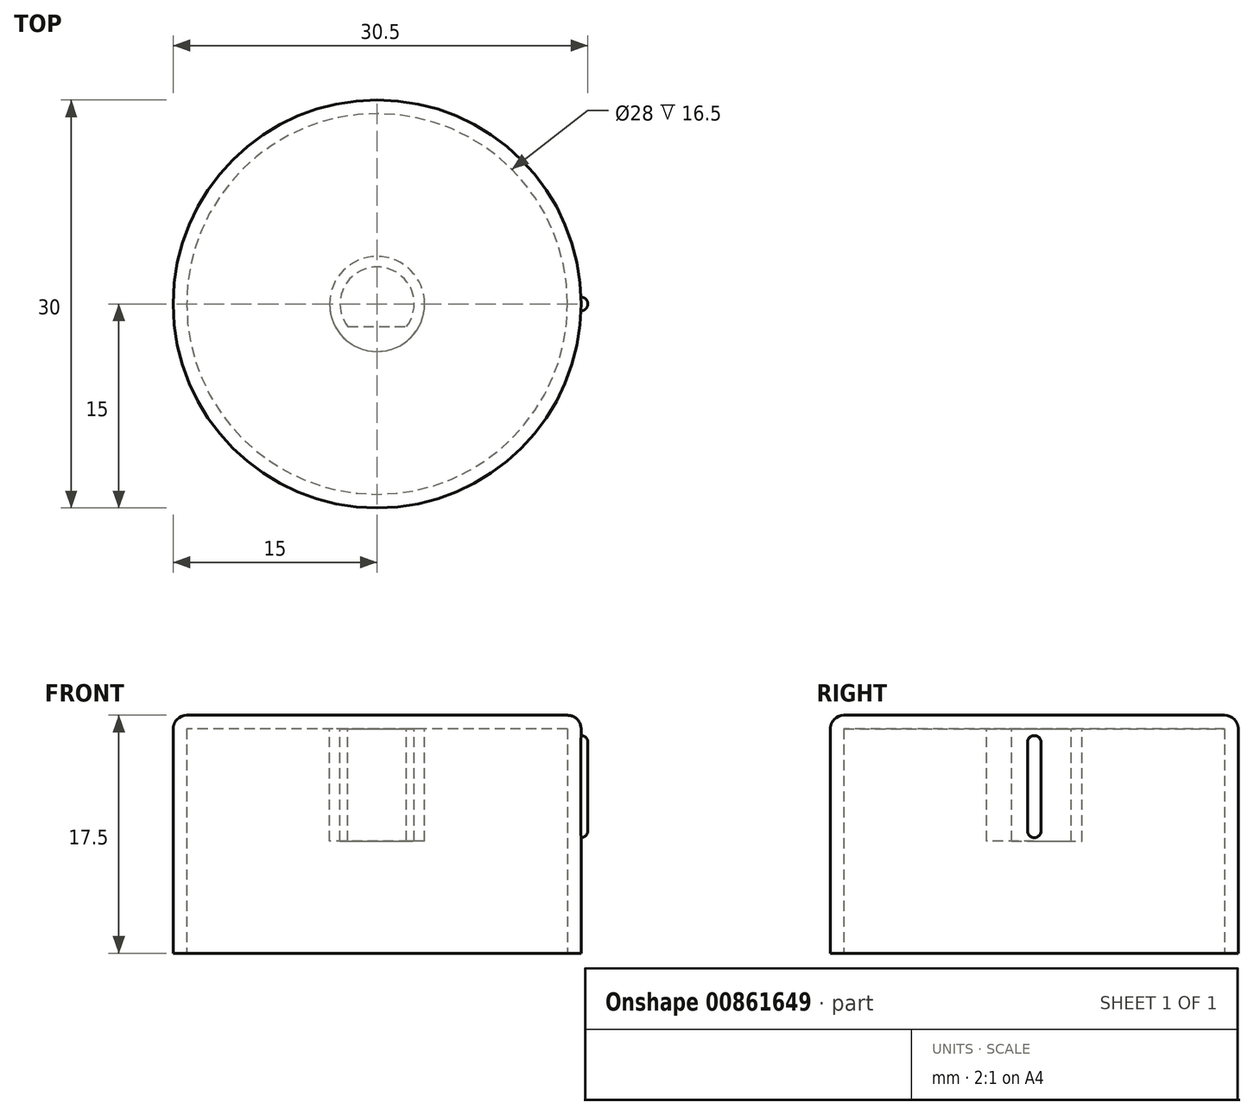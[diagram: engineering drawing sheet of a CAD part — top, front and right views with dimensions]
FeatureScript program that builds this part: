
annotation { "Feature Type Name" : "Feature", "Feature Type Description" : "" }
export const myFeature = defineFeature(function(context is Context, id is Id, definition is map)
    precondition{}
    {
        {
            var Q0;
            Q0=qCreatedBy(makeId("Top.planeOp"),FACE);
            var sketch = newSketch(context, id + "F0", { "sketchPlane" : qUnion([Q0])});
            skCircle(sketch, "E0", {"center": v(0, 0) * mm, "radius": 15 * mm});
            skSolve(sketch);
        }
        {
            var Q0;
            Q0 = qSketchRegion(id + "F0", true);
            extrude(context, id + "F1", {"entities" : qUnion([Q0]), "depth" : 17.5 * mm, "offsetDistance" : 25 * mm});
        }
        {
            var Q0;
            Q0=makeQuery(id+"F1.opExtrude","CAP_FACE",FACE,{"disambiguationData":[OSD([sQuery(id+"F0.wireOp",EDGE,"E0")])],"isStart":true});
            shell(context, id + "F2", {"entities" : qUnion([Q0]), "thickness" : 1 * mm});
        }
        {
            var Q0;
            {var subQ0=sQuery(id+"F0.wireOp",EDGE,"E0");Q0=makeQuery(id+"F2.opShell","OFFSET_FACE",FACE,{"disambiguationData":[OSD([subQ0]),TDD([makeQuery(id+"F1.opExtrude","CAP_FACE",FACE,{"disambiguationData":[OSD([subQ0])],"isStart":false})])]});}
            var sketch = newSketch(context, id + "F3", { "sketchPlane" : qUnion([Q0])});
            skCircle(sketch, "E1", {"center": v(0, 0) * mm, "radius": 3.5 * mm});
            skArc(sketch, "E2", {"start": v(-2.15, 1.67) * mm, "mid": v(0, -2.73) * mm, "end": v(2.15, 1.67) * mm});
            skLineSegment(sketch, "E3", {"start": v(-2.15, 1.67) * mm, "end": v(2.15, 1.67) * mm});
            skSolve(sketch);
        }
        {
            var Q0;
            Q0=makeQuery(id+"F3.imprint","IMPRINT",FACE,{"disambiguationData":[TD([[makeQuery(id+"F3.imprint","IMPRINT",EDGE,{"derivedFrom":sQuery(id+"F3.wireOp",EDGE,"E1")}),1.0]])]});
            extrude(context, id + "F4", {"entities" : qUnion([Q0]), "operationType" : NewBodyOperationType.ADD, "depth" : 8.25 * mm, "offsetDistance" : 25 * mm});
        }
        {
            var Q0;
            Q0=makeQuery(id+"F1.opExtrude","CAP_EDGE",EDGE,{"disambiguationData":[OSD([sQuery(id+"F0.wireOp",EDGE,"E0")])],"isStart":false});
            fillet(context, id + "F5", {"entities" : qUnion([Q0]), "radius" : 1 * mm, "tangentPropagation" : true, "allowEdgeOverflow" : false});
        }
        {
            var Q0;
            Q0=qCreatedBy(makeId("Right.planeOp"),FACE);
            cPlane(context, id + "F6", {"entities" : qUnion([Q0]), "cplaneType" : CPlaneType.OFFSET, "offset" : 15 * mm, "width" : 150 * mm, "height" : 150 * mm});
        }
        {
            var Q0;
            Q0=qCreatedBy(id+"F6.planeOp",FACE);
            var sketch = newSketch(context, id + "F7", { "sketchPlane" : qUnion([Q0])});
            skLineSegment(sketch, "E4.left", {"start": v(0.5, 15.5) * mm, "end": v(0.5, 9) * mm});
            skLineSegment(sketch, "E4.right", {"start": v(-0.5, 15.5) * mm, "end": v(-0.5, 9) * mm});
            skPoint(sketch, "E4.middle", {"position": v(0, 12.25) * mm});
            skArc(sketch, "E5", {"start": v(0.5, 15.5) * mm, "mid": v(0, 16) * mm, "end": v(-0.5, 15.5) * mm});
            skArc(sketch, "E6", {"start": v(-0.5, 9) * mm, "mid": v(0, 8.5) * mm, "end": v(0.5, 9) * mm});
            skSolve(sketch);
        }
        {
            var Q0;
            Q0=makeQuery(id+"F7.imprint","IMPRINT",FACE,{"disambiguationData":[TD([[makeQuery(id+"F7.imprint","IMPRINT",EDGE,{"derivedFrom":sQuery(id+"F7.wireOp",EDGE,"E4.left")}),-1.0]])]});
            var Q1;
            Q1=sQuery(id+"F7.wireOp",EDGE,"E4.right");
            var Q2;
            Q2=sQuery(id+"F7.wireOp",EDGE,"E4.left");
            var Q3;
            Q3=sQuery(id+"F7.wireOp",EDGE,"E5");
            var Q4;
            Q4=sQuery(id+"F7.wireOp",EDGE,"E6");
            extrude(context, id + "F8", {"entities" : qUnion([Q0]), "operationType" : NewBodyOperationType.ADD, "surfaceEntities" : qUnion([Q1, Q2, Q3, Q4]), "depth" : .5 * mm, "offsetDistance" : 25 * mm});
        }
        {
            var Q0;
            Q0=makeQuery(id+"F8.opExtrude","CAP_EDGE",EDGE,{"disambiguationData":[OSD([sQuery(id+"F7.wireOp",EDGE,"E4.right")])],"isStart":false});
            fillet(context, id + "F9", {"entities" : qUnion([Q0]), "radius" : .5 * mm, "tangentPropagation" : true, "allowEdgeOverflow" : false});
        }
    });
